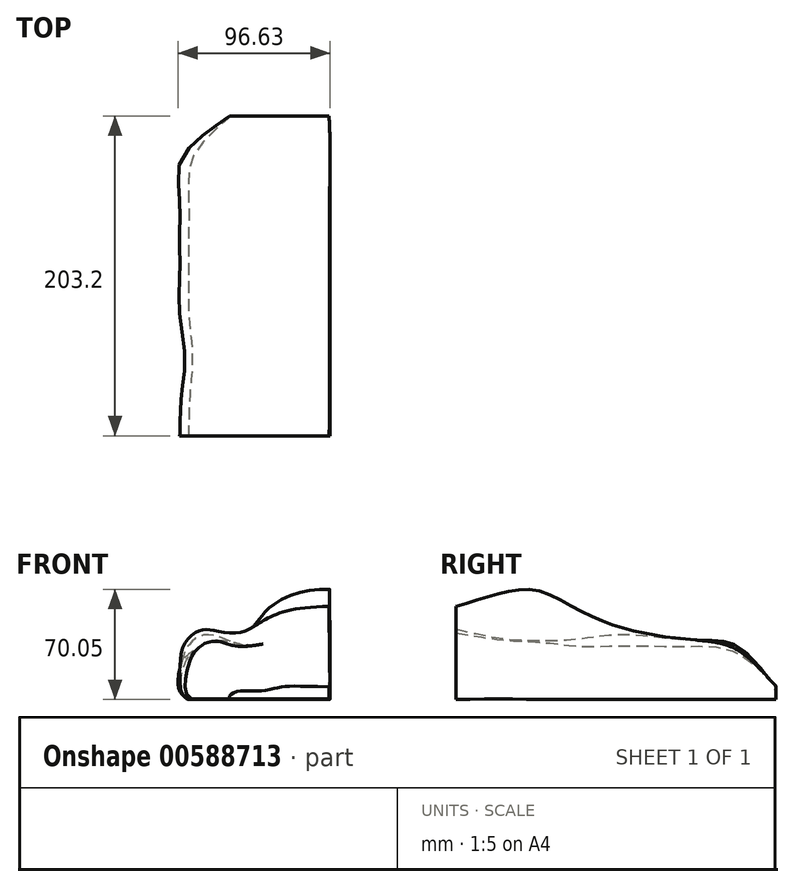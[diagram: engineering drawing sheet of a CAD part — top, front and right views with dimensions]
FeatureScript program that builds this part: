
annotation { "Feature Type Name" : "Feature", "Feature Type Description" : "" }
export const myFeature = defineFeature(function(context is Context, id is Id, definition is map)
    precondition{}
    {
        {
            var Q0;
            Q0=qCreatedBy(makeId("Front.planeOp"),FACE);
            cPlane(context, id + "F0", {"entities" : qUnion([Q0]), "cplaneType" : CPlaneType.OFFSET, "offset" : 48.26 * mm, "width" : 152.4 * mm, "height" : 152.4 * mm});
        }
        {
            var Q0;
            Q0=qCreatedBy(id+"F0.planeOp",FACE);
            cPlane(context, id + "F1", {"entities" : qUnion([Q0]), "cplaneType" : CPlaneType.OFFSET, "offset" : 5.33 * mm, "width" : 152.4 * mm, "height" : 152.4 * mm});
        }
        {
            var Q0;
            Q0=qCreatedBy(id+"F1.planeOp",FACE);
            cPlane(context, id + "F2", {"entities" : qUnion([Q0]), "cplaneType" : CPlaneType.OFFSET, "offset" : 25.4 * mm, "width" : 152.4 * mm, "height" : 152.4 * mm});
        }
        {
            var Q0;
            Q0=qCreatedBy(id+"F2.planeOp",FACE);
            cPlane(context, id + "F3", {"entities" : qUnion([Q0]), "cplaneType" : CPlaneType.OFFSET, "offset" : 25.4 * mm, "width" : 152.4 * mm, "height" : 152.4 * mm});
        }
        {
            var Q0;
            Q0=qCreatedBy(id+"F3.planeOp",FACE);
            cPlane(context, id + "F4", {"entities" : qUnion([Q0]), "cplaneType" : CPlaneType.OFFSET, "offset" : 25.4 * mm, "width" : 152.4 * mm, "height" : 152.4 * mm});
        }
        {
            var Q0;
            Q0=qCreatedBy(id+"F4.planeOp",FACE);
            cPlane(context, id + "F5", {"entities" : qUnion([Q0]), "cplaneType" : CPlaneType.OFFSET, "offset" : 25.4 * mm, "width" : 152.4 * mm, "height" : 152.4 * mm});
        }
        {
            var Q0;
            Q0=qCreatedBy(id+"F5.planeOp",FACE);
            cPlane(context, id + "F6", {"entities" : qUnion([Q0]), "cplaneType" : CPlaneType.OFFSET, "offset" : 25.4 * mm, "width" : 152.4 * mm, "height" : 152.4 * mm});
        }
        {
            var Q0;
            Q0=qCreatedBy(id+"F6.planeOp",FACE);
            cPlane(context, id + "F7", {"entities" : qUnion([Q0]), "cplaneType" : CPlaneType.OFFSET, "offset" : 25.4 * mm, "width" : 152.4 * mm, "height" : 152.4 * mm});
        }
        {
            var Q0;
            Q0=qCreatedBy(id+"F7.planeOp",FACE);
            cPlane(context, id + "F8", {"entities" : qUnion([Q0]), "cplaneType" : CPlaneType.OFFSET, "offset" : 25.4 * mm, "width" : 152.4 * mm, "height" : 152.4 * mm});
        }
        {
            var Q0;
            Q0=qCreatedBy(id+"F8.planeOp",FACE);
            cPlane(context, id + "F9", {"entities" : qUnion([Q0]), "cplaneType" : CPlaneType.OFFSET, "offset" : 25.4 * mm, "width" : 152.4 * mm, "height" : 152.4 * mm});
        }
        {
            var Q0;
            Q0=qCreatedBy(id+"F2.planeOp",FACE);
            var sketch = newSketch(context, id + "F10", { "sketchPlane" : qUnion([Q0])});
            skFitSpline(sketch, "E0", {"points": [v(35.98, -2.22) * mm, v(-9.96, -3.7) * mm, v(-25.6, 0) * mm, v(-41.25, -5.03) * mm, v(-53.57, -9.69) * mm, v(-57.57, -23.67) * mm, v(-50.9, -33.99) * mm], "startDerivative": vector(-420.37, 0) * mm, "endDerivative": vector(119.07, -72.77) * mm});
            skFitSpline(sketch, "E1", {"points": [v(-50.9, -33.99) * mm, v(35.78, -33.99) * mm], "startDerivative": vector(101.97, 0) * mm, "endDerivative": vector(101.97, 0) * mm});
            skFitSpline(sketch, "E2", {"points": [v(35.78, -33.99) * mm, v(35.98, -2.22) * mm], "startDerivative": vector(0.6, 26.4) * mm, "endDerivative": vector(0, 32.96) * mm});
            skSolve(sketch);
        }
        {
            var Q0;
            Q0=qCreatedBy(id+"F3.planeOp",FACE);
            var sketch = newSketch(context, id + "F11", { "sketchPlane" : qUnion([Q0])});
            skFitSpline(sketch, "E3", {"points": [v(35.64, 3.63) * mm, v(-20.95, 0) * mm, v(-36.26, 3.3) * mm, v(-46.91, 0) * mm, v(-54.24, -7.02) * mm, v(-59.52, -21.54) * mm, v(-53.92, -34.14) * mm], "startDerivative": vector(-420.37, 0) * mm, "endDerivative": vector(119.07, -72.77) * mm});
            skFitSpline(sketch, "E4", {"points": [v(-53.92, -34.14) * mm, v(35.74, -34.14) * mm], "startDerivative": vector(101.97, 0) * mm, "endDerivative": vector(101.97, 0) * mm});
            skFitSpline(sketch, "E5", {"points": [v(35.74, -34.14) * mm, v(35.64, 3.63) * mm], "startDerivative": vector(0, 87.62) * mm, "endDerivative": vector(0, 87.62) * mm});
            skSolve(sketch);
        }
        {
            var Q0;
            Q0=qCreatedBy(id+"F4.planeOp",FACE);
            var sketch = newSketch(context, id + "F12", { "sketchPlane" : qUnion([Q0])});
            skFitSpline(sketch, "E6", {"points": [v(35.64, 6.62) * mm, v(-20.62, 0) * mm, v(-35.6, 4.96) * mm, v(-48.24, 3.63) * mm, v(-55.24, -4.03) * mm, v(-59.52, -21.54) * mm, v(-53.92, -34.14) * mm], "startDerivative": vector(-372.85, -13.93) * mm, "endDerivative": vector(119.07, -72.77) * mm});
            skFitSpline(sketch, "E7", {"points": [v(-53.92, -34.14) * mm, v(35.74, -34.14) * mm], "startDerivative": vector(101.97, 0) * mm, "endDerivative": vector(101.97, 0) * mm});
            skFitSpline(sketch, "E8", {"points": [v(35.74, -34.14) * mm, v(35.64, 6.62) * mm], "startDerivative": vector(0, 87.62) * mm, "endDerivative": vector(0, 87.62) * mm});
            skSolve(sketch);
        }
        {
            var Q0;
            Q0=qCreatedBy(id+"F5.planeOp",FACE);
            var sketch = newSketch(context, id + "F13", { "sketchPlane" : qUnion([Q0])});
            skFitSpline(sketch, "E9", {"points": [v(35.64, 12.62) * mm, v(-18.62, 0) * mm, v(-37.26, 6.3) * mm, v(-47.25, 5.63) * mm, v(-55.9, -3.03) * mm, v(-59.52, -21.54) * mm, v(-53.92, -34.14) * mm], "startDerivative": vector(-420.37, 0) * mm, "endDerivative": vector(119.07, -72.77) * mm});
            skFitSpline(sketch, "E10", {"points": [v(-53.92, -34.14) * mm, v(35.74, -34.14) * mm], "startDerivative": vector(101.97, 0) * mm, "endDerivative": vector(101.97, 0) * mm});
            skFitSpline(sketch, "E11", {"points": [v(35.74, -34.14) * mm, v(35.64, 12.62) * mm], "startDerivative": vector(0, 87.62) * mm, "endDerivative": vector(0, 87.62) * mm});
            skSolve(sketch);
        }
        {
            var Q0;
            Q0=qCreatedBy(id+"F6.planeOp",FACE);
            var sketch = newSketch(context, id + "F14", { "sketchPlane" : qUnion([Q0])});
            skFitSpline(sketch, "E12", {"points": [v(35.64, 23.6) * mm, v(-19.62, 0) * mm, v(-39.59, 3.96) * mm, v(-49.58, 0) * mm, v(-55.57, -7.02) * mm, v(-59.52, -21.54) * mm, v(-53.92, -34.14) * mm], "startDerivative": vector(-420.37, 0) * mm, "endDerivative": vector(119.07, -72.77) * mm});
            skFitSpline(sketch, "E13", {"points": [v(-53.92, -34.14) * mm, v(35.74, -34.14) * mm], "startDerivative": vector(101.97, 0) * mm, "endDerivative": vector(101.97, 0) * mm});
            skFitSpline(sketch, "E14", {"points": [v(35.74, -34.14) * mm, v(35.64, 23.6) * mm], "startDerivative": vector(0, 87.62) * mm, "endDerivative": vector(0, 87.62) * mm});
            skSolve(sketch);
        }
        {
            var Q0;
            Q0=qCreatedBy(id+"F7.planeOp",FACE);
            var sketch = newSketch(context, id + "F15", { "sketchPlane" : qUnion([Q0])});
            skFitSpline(sketch, "E15", {"points": [v(35.64, 35.25) * mm, v(-17.95, 4.63) * mm, v(-37.6, 2.96) * mm, v(-46.25, 0) * mm, v(-52.57, -7.7) * mm, v(-56.23, -24) * mm, v(-51.57, -33.99) * mm], "startDerivative": vector(-420.37, 0) * mm, "endDerivative": vector(119.07, -72.77) * mm});
            skFitSpline(sketch, "E16", {"points": [v(-51.57, -33.99) * mm, v(35.74, -33.99) * mm], "startDerivative": vector(101.97, 0) * mm, "endDerivative": vector(101.97, 0) * mm});
            skFitSpline(sketch, "E17", {"points": [v(35.74, -33.99) * mm, v(35.64, 35.25) * mm], "startDerivative": vector(0, 87.62) * mm, "endDerivative": vector(0, 87.62) * mm});
            skSolve(sketch);
        }
        {
            var Q0;
            Q0=qCreatedBy(id+"F8.planeOp",FACE);
            var sketch = newSketch(context, id + "F16", { "sketchPlane" : qUnion([Q0])});
            skFitSpline(sketch, "E18", {"points": [v(35.64, 32.59) * mm, v(-18.62, 6.62) * mm, v(-36.6, 4.63) * mm, v(-46.91, 4.3) * mm, v(-51.57, 0) * mm, v(-58.23, -23.34) * mm, v(-53.24, -33.66) * mm], "startDerivative": vector(-420.37, 0) * mm, "endDerivative": vector(119.07, -72.77) * mm});
            skFitSpline(sketch, "E19", {"points": [v(-53.24, -33.66) * mm, v(35.74, -33.66) * mm], "startDerivative": vector(101.97, 0) * mm, "endDerivative": vector(101.97, 0) * mm});
            skFitSpline(sketch, "E20", {"points": [v(35.74, -33.66) * mm, v(35.64, 32.59) * mm], "startDerivative": vector(0, 87.62) * mm, "endDerivative": vector(0, 87.62) * mm});
            skSolve(sketch);
        }
        {
            var Q0;
            Q0=qCreatedBy(id+"F9.planeOp",FACE);
            var sketch = newSketch(context, id + "F17", { "sketchPlane" : qUnion([Q0])});
            skFitSpline(sketch, "E21", {"points": [v(35.31, 24.93) * mm, v(-18.95, 8.95) * mm, v(-37.6, 9.62) * mm, v(-46.64, 9.81) * mm, v(-57, 0.2) * mm, v(-59.52, -21.54) * mm, v(-53.92, -34.14) * mm], "startDerivative": vector(-420.37, 0) * mm, "endDerivative": vector(119.07, -72.77) * mm});
            skFitSpline(sketch, "E22", {"points": [v(-53.92, -34.14) * mm, v(35.74, -34.14) * mm], "startDerivative": vector(101.97, 0) * mm, "endDerivative": vector(101.97, 0) * mm});
            skFitSpline(sketch, "E23", {"points": [v(35.74, -34.14) * mm, v(35.31, 24.93) * mm], "startDerivative": vector(0, 87.62) * mm, "endDerivative": vector(0, 87.62) * mm});
            skSolve(sketch);
        }
        {
            var Q0;
            Q0=qCreatedBy(id+"F1.planeOp",FACE);
            var sketch = newSketch(context, id + "F18", { "sketchPlane" : qUnion([Q0])});
            skFitSpline(sketch, "E24", {"points": [v(35.26, -26) * mm, v(5.32, -26.06) * mm, v(-5.15, -28.3) * mm, v(-17.04, -28.65) * mm, v(-25.4, -29.83) * mm, v(-27.98, -32.3) * mm, v(-27.05, -34.17) * mm], "startDerivative": vector(-193.7, 0.7) * mm, "endDerivative": vector(20.1, -50.72) * mm});
            skFitSpline(sketch, "E25", {"points": [v(-27.05, -34.17) * mm, v(35.05, -34.17) * mm], "startDerivative": vector(101.97, 0) * mm, "endDerivative": vector(101.97, 0) * mm});
            skFitSpline(sketch, "E26", {"points": [v(35.05, -34.17) * mm, v(35.26, -26) * mm], "startDerivative": vector(0.61, 10.62) * mm, "endDerivative": vector(0, 19) * mm});
            skSolve(sketch);
        }
        {
            var Q0;
            Q0=qCreatedBy(id+"F0.planeOp",FACE);
            var sketch = newSketch(context, id + "F19", { "sketchPlane" : qUnion([Q0])});
            skFitSpline(sketch, "E27", {"points": [v(35.67, -32.8) * mm, v(31.75, -32.8) * mm, v(29.02, -32.88) * mm, v(25.24, -32.95) * mm, v(22.07, -32.93) * mm, v(18.66, -33.37) * mm, v(18.38, -34.14) * mm], "startDerivative": vector(-5.4, 0.3) * mm, "endDerivative": vector(28.92, -11.13) * mm});
            skFitSpline(sketch, "E28", {"points": [v(18.38, -34.14) * mm, v(35.68, -34.14) * mm], "startDerivative": vector(47.94, 0) * mm, "endDerivative": vector(33.49, 0) * mm});
            skFitSpline(sketch, "E29", {"points": [v(35.68, -34.14) * mm, v(35.67, -32.8) * mm], "startDerivative": vector(-0.05, 6.5) * mm, "endDerivative": vector(0, 5.76) * mm});
            skSolve(sketch);
        }
        {
            var Q0;
            Q0 = qSketchRegion(id + "F10", true);
            var Q1;
            Q1 = qSketchRegion(id + "F11", true);
            var Q2;
            Q2 = qSketchRegion(id + "F12", true);
            var Q3;
            Q3 = qSketchRegion(id + "F13", true);
            var Q4;
            Q4 = qSketchRegion(id + "F14", true);
            var Q5;
            Q5 = qSketchRegion(id + "F15", true);
            var Q6;
            Q6 = qSketchRegion(id + "F16", true);
            var Q7;
            Q7 = qSketchRegion(id + "F17", true);
            var Q8;
            Q8 = qSketchRegion(id + "F18", true);
            var Q9;
            Q9 = qSketchRegion(id + "F19", true);
            var Q10;
            Q10 = qConstructionFilter(qBodyType(qCreatedBy(id + "F18" ,EDGE), BodyType.WIRE), ConstructionObject.NO);
            var Q11;
            Q11 = qConstructionFilter(qBodyType(qCreatedBy(id + "F10" ,EDGE), BodyType.WIRE), ConstructionObject.NO);
            var Q12;
            Q12 = qConstructionFilter(qBodyType(qCreatedBy(id + "F11" ,EDGE), BodyType.WIRE), ConstructionObject.NO);
            var Q13;
            Q13 = qConstructionFilter(qBodyType(qCreatedBy(id + "F12" ,EDGE), BodyType.WIRE), ConstructionObject.NO);
            var Q14;
            Q14 = qConstructionFilter(qBodyType(qCreatedBy(id + "F13" ,EDGE), BodyType.WIRE), ConstructionObject.NO);
            var Q15;
            Q15 = qConstructionFilter(qBodyType(qCreatedBy(id + "F14" ,EDGE), BodyType.WIRE), ConstructionObject.NO);
            var Q16;
            Q16 = qConstructionFilter(qBodyType(qCreatedBy(id + "F15" ,EDGE), BodyType.WIRE), ConstructionObject.NO);
            var Q17;
            Q17 = qConstructionFilter(qBodyType(qCreatedBy(id + "F16" ,EDGE), BodyType.WIRE), ConstructionObject.NO);
            var Q18;
            Q18 = qConstructionFilter(qBodyType(qCreatedBy(id + "F17" ,EDGE), BodyType.WIRE), ConstructionObject.NO);
            loft(context, id + "F20", {"bodyType" : ToolBodyType.SURFACE, "sheetProfilesArray" : [{ "sheetProfileEntities" : qUnion([Q0]) }, { "sheetProfileEntities" : qUnion([Q1]) }, { "sheetProfileEntities" : qUnion([Q2]) }, { "sheetProfileEntities" : qUnion([Q3]) }, { "sheetProfileEntities" : qUnion([Q4]) }, { "sheetProfileEntities" : qUnion([Q5]) }, { "sheetProfileEntities" : qUnion([Q6]) }, { "sheetProfileEntities" : qUnion([Q7]) }, { "sheetProfileEntities" : qUnion([Q8]) }, { "sheetProfileEntities" : qUnion([Q9]) }], "wireProfilesArray" : [{ "wireProfileEntities" : qUnion([Q10]) }, { "wireProfileEntities" : qUnion([Q11]) }, { "wireProfileEntities" : qUnion([Q12]) }, { "wireProfileEntities" : qUnion([Q13]) }, { "wireProfileEntities" : qUnion([Q14]) }, { "wireProfileEntities" : qUnion([Q15]) }, { "wireProfileEntities" : qUnion([Q16]) }, { "wireProfileEntities" : qUnion([Q17]) }, { "wireProfileEntities" : qUnion([Q18]) }]});
        }
    });
